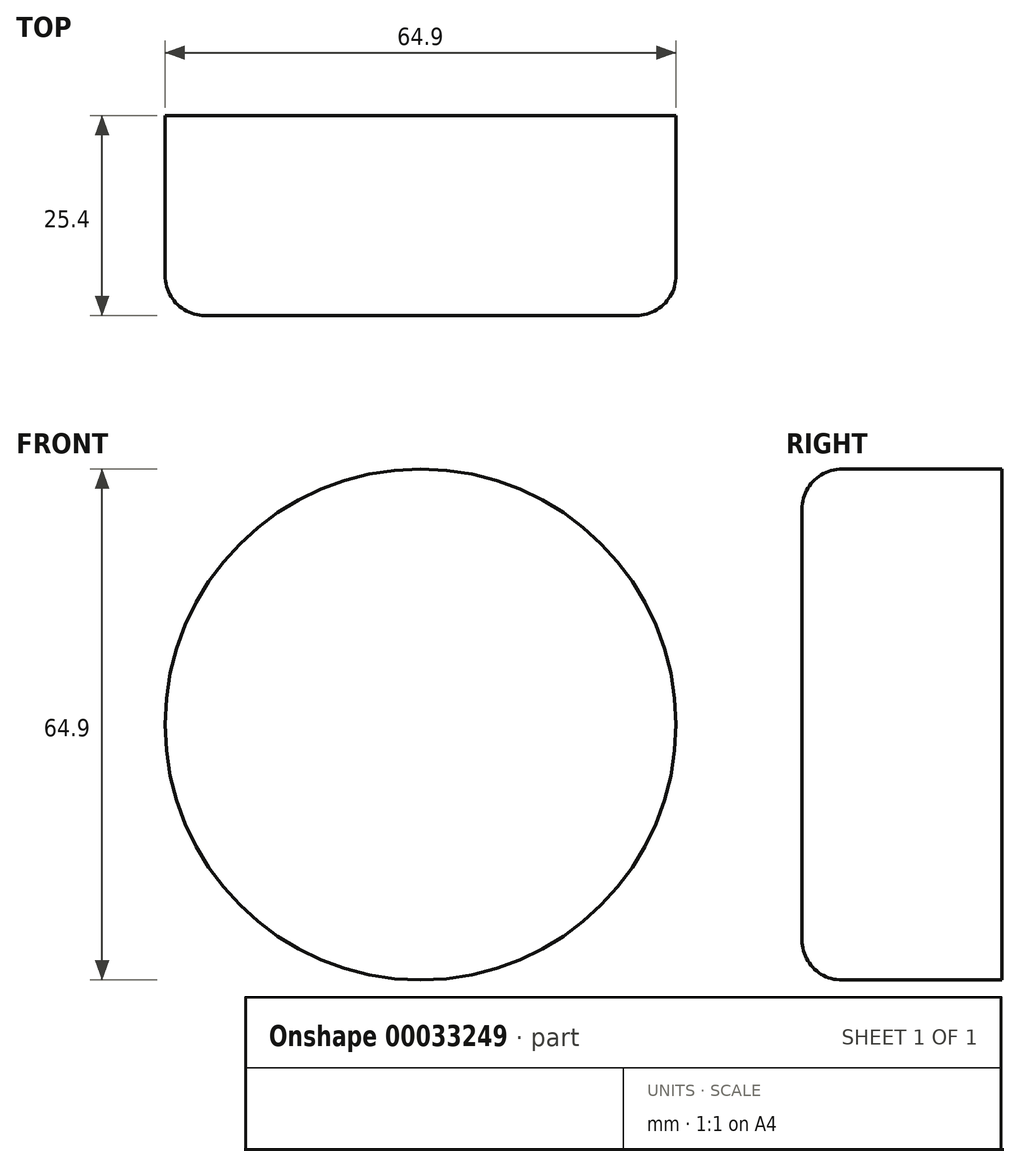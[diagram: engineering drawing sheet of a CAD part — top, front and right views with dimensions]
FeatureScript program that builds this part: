
annotation { "Feature Type Name" : "Feature", "Feature Type Description" : "" }
export const myFeature = defineFeature(function(context is Context, id is Id, definition is map)
    precondition{}
    {
        {
            var Q0;
            Q0=qCreatedBy(makeId("Front.planeOp"),FACE);
            var sketch = newSketch(context, id + "F0", { "sketchPlane" : qUnion([Q0])});
            skCircle(sketch, "E0", {"center": v(0, 0) * mm, "radius": 32.45 * mm});
            skSolve(sketch);
        }
        {
            var Q0;
            Q0 = qSketchRegion(id + "F0", true);
            extrude(context, id + "F1", {"entities" : qUnion([Q0]), "depth" : 25.4 * mm});
        }
        {
            var Q0;
            Q0=makeQuery(id+"F1.opExtrude","CAP_EDGE",EDGE,{"disambiguationData":[OSD([sQuery(id+"F0.wireOp",EDGE,"E0")])],"isStart":false});
            fillet(context, id + "F2", {"entities" : qUnion([Q0]), "radius" : 5.08 * mm, "tangentPropagation" : true, "allowEdgeOverflow" : false});
        }
    });
